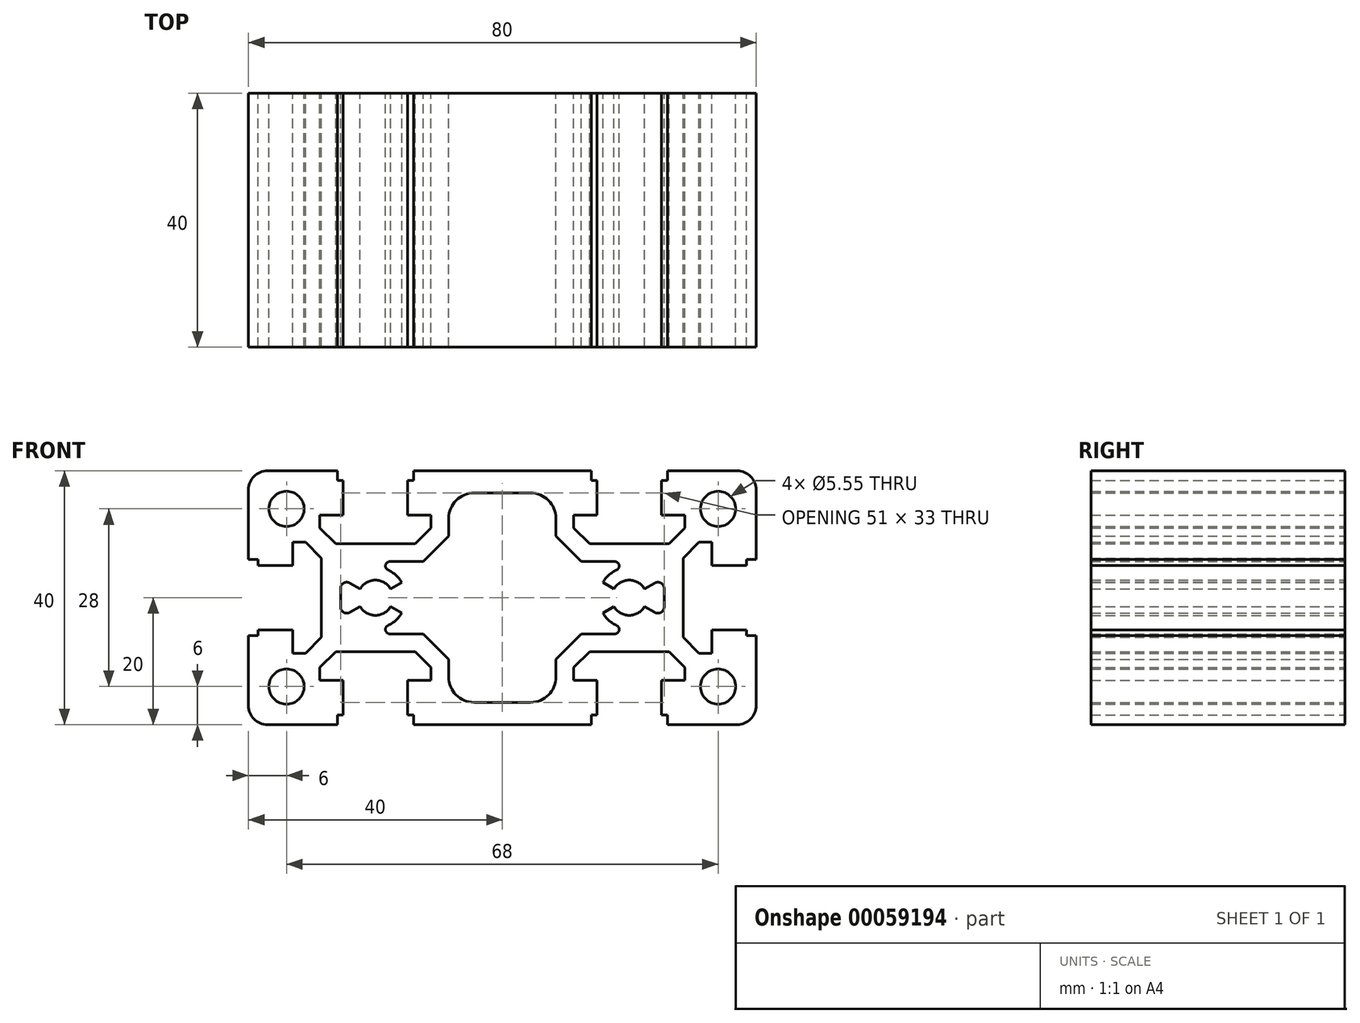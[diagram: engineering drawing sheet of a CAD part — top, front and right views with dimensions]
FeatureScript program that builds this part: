
annotation { "Feature Type Name" : "Feature", "Feature Type Description" : "" }
export const myFeature = defineFeature(function(context is Context, id is Id, definition is map)
    precondition{}
    {
        {
            assignVariable(context, id + "F0", {"name" : "Config", "anyValue" : 0});
        }
        {
            assignVariable(context, id + "F1", {"name" : "Length", "anyValue" : [40, 80, 120, 200, 500][getVariable(context, 'Config')]});
        }
        {
            var Q0;
            Q0=qCreatedBy(makeId("Front.planeOp"),FACE);
            var sketch = newSketch(context, id + "F2", { "sketchPlane" : qUnion([Q0])});
            skLineSegment(sketch, "E0", {"start": v(19.96, 21.75) * mm, "end": v(25.78, 21.75) * mm});
            skLineSegment(sketch, "E1", {"start": v(22.87, 18.84) * mm, "end": v(22.87, 24.66) * mm});
            skLineSegment(sketch, "E2", {"start": v(19.96, 49.75) * mm, "end": v(25.78, 49.75) * mm});
            skLineSegment(sketch, "E3", {"start": v(22.87, 46.84) * mm, "end": v(22.87, 52.66) * mm});
            skLineSegment(sketch, "E4", {"start": v(-48.04, 21.75) * mm, "end": v(-42.22, 21.75) * mm});
            skLineSegment(sketch, "E5", {"start": v(-45.13, 18.84) * mm, "end": v(-45.13, 24.66) * mm});
            skLineSegment(sketch, "E6", {"start": v(-48.04, 49.75) * mm, "end": v(-42.22, 49.75) * mm});
            skLineSegment(sketch, "E7", {"start": v(-45.13, 46.84) * mm, "end": v(-45.13, 52.66) * mm});
            skArc(sketch, "E8", {"start": v(-48.13, 55.75) * mm, "mid": v(-50.25, 54.87) * mm, "end": v(-51.13, 52.75) * mm});
            skLineSegment(sketch, "E9", {"start": v(-51.13, 52.75) * mm, "end": v(-51.13, 41.75) * mm});
            skLineSegment(sketch, "E10", {"start": v(-51.13, 41.75) * mm, "end": v(-49.63, 41.75) * mm});
            skLineSegment(sketch, "E11", {"start": v(-49.63, 41.75) * mm, "end": v(-49.63, 40.85) * mm});
            skLineSegment(sketch, "E12", {"start": v(-49.63, 40.85) * mm, "end": v(-44.13, 40.85) * mm});
            skLineSegment(sketch, "E13", {"start": v(-44.13, 40.85) * mm, "end": v(-44.13, 44.5) * mm});
            skLineSegment(sketch, "E14", {"start": v(-44.13, 44.5) * mm, "end": v(-42.13, 44.5) * mm});
            skLineSegment(sketch, "E15", {"start": v(-42.13, 44.5) * mm, "end": v(-39.63, 42) * mm});
            skLineSegment(sketch, "E16", {"start": v(-39.63, 42) * mm, "end": v(-39.63, 29.5) * mm});
            skLineSegment(sketch, "E17", {"start": v(-39.63, 29.5) * mm, "end": v(-42.13, 27) * mm});
            skLineSegment(sketch, "E18", {"start": v(-42.13, 27) * mm, "end": v(-44.13, 27) * mm});
            skLineSegment(sketch, "E19", {"start": v(-44.13, 27) * mm, "end": v(-44.13, 30.65) * mm});
            skLineSegment(sketch, "E20", {"start": v(-44.13, 30.65) * mm, "end": v(-49.63, 30.65) * mm});
            skLineSegment(sketch, "E21", {"start": v(-49.63, 30.65) * mm, "end": v(-49.63, 29.75) * mm});
            skLineSegment(sketch, "E22", {"start": v(-49.63, 29.75) * mm, "end": v(-51.13, 29.75) * mm});
            skLineSegment(sketch, "E23", {"start": v(-51.13, 29.75) * mm, "end": v(-51.13, 18.75) * mm});
            skArc(sketch, "E24", {"start": v(-51.13, 18.75) * mm, "mid": v(-50.25, 16.63) * mm, "end": v(-48.13, 15.75) * mm});
            skLineSegment(sketch, "E25", {"start": v(-48.13, 15.75) * mm, "end": v(-37.13, 15.75) * mm});
            skLineSegment(sketch, "E26", {"start": v(-37.13, 15.75) * mm, "end": v(-37.13, 17.25) * mm});
            skLineSegment(sketch, "E27", {"start": v(-37.13, 17.25) * mm, "end": v(-36.23, 17.25) * mm});
            skLineSegment(sketch, "E28", {"start": v(-36.23, 17.25) * mm, "end": v(-36.23, 22.75) * mm});
            skLineSegment(sketch, "E29", {"start": v(-36.23, 22.75) * mm, "end": v(-39.88, 22.75) * mm});
            skLineSegment(sketch, "E30", {"start": v(-39.88, 22.75) * mm, "end": v(-39.88, 24.75) * mm});
            skLineSegment(sketch, "E31", {"start": v(-39.88, 24.75) * mm, "end": v(-37.38, 27.25) * mm});
            skLineSegment(sketch, "E32", {"start": v(-37.38, 27.25) * mm, "end": v(-24.88, 27.25) * mm});
            skLineSegment(sketch, "E33", {"start": v(-24.88, 27.25) * mm, "end": v(-22.38, 24.75) * mm});
            skLineSegment(sketch, "E34", {"start": v(-22.38, 24.75) * mm, "end": v(-22.38, 22.75) * mm});
            skLineSegment(sketch, "E35", {"start": v(-22.38, 22.75) * mm, "end": v(-26.03, 22.75) * mm});
            skLineSegment(sketch, "E36", {"start": v(-26.03, 22.75) * mm, "end": v(-26.03, 17.25) * mm});
            skLineSegment(sketch, "E37", {"start": v(-26.03, 17.25) * mm, "end": v(-25.13, 17.25) * mm});
            skLineSegment(sketch, "E38", {"start": v(-25.13, 17.25) * mm, "end": v(-25.13, 15.75) * mm});
            skLineSegment(sketch, "E39", {"start": v(-25.13, 15.75) * mm, "end": v(2.87, 15.75) * mm});
            skLineSegment(sketch, "E40", {"start": v(2.87, 15.75) * mm, "end": v(2.87, 17.25) * mm});
            skLineSegment(sketch, "E41", {"start": v(2.87, 17.25) * mm, "end": v(3.77, 17.25) * mm});
            skLineSegment(sketch, "E42", {"start": v(3.77, 17.25) * mm, "end": v(3.77, 22.75) * mm});
            skLineSegment(sketch, "E43", {"start": v(3.77, 22.75) * mm, "end": v(0.12, 22.75) * mm});
            skLineSegment(sketch, "E44", {"start": v(0.12, 22.75) * mm, "end": v(0.12, 24.75) * mm});
            skLineSegment(sketch, "E45", {"start": v(0.12, 24.75) * mm, "end": v(2.62, 27.25) * mm});
            skLineSegment(sketch, "E46", {"start": v(2.62, 27.25) * mm, "end": v(15.12, 27.25) * mm});
            skLineSegment(sketch, "E47", {"start": v(15.12, 27.25) * mm, "end": v(17.62, 24.75) * mm});
            skLineSegment(sketch, "E48", {"start": v(17.62, 24.75) * mm, "end": v(17.62, 22.75) * mm});
            skLineSegment(sketch, "E49", {"start": v(17.62, 22.75) * mm, "end": v(13.97, 22.75) * mm});
            skLineSegment(sketch, "E50", {"start": v(13.97, 22.75) * mm, "end": v(13.97, 17.25) * mm});
            skLineSegment(sketch, "E51", {"start": v(13.97, 17.25) * mm, "end": v(14.87, 17.25) * mm});
            skLineSegment(sketch, "E52", {"start": v(14.87, 17.25) * mm, "end": v(14.87, 15.75) * mm});
            skLineSegment(sketch, "E53", {"start": v(14.87, 15.75) * mm, "end": v(25.87, 15.75) * mm});
            skArc(sketch, "E54", {"start": v(25.87, 15.75) * mm, "mid": v(28, 16.63) * mm, "end": v(28.87, 18.75) * mm});
            skLineSegment(sketch, "E55", {"start": v(28.87, 18.75) * mm, "end": v(28.87, 29.75) * mm});
            skLineSegment(sketch, "E56", {"start": v(28.87, 29.75) * mm, "end": v(27.37, 29.75) * mm});
            skLineSegment(sketch, "E57", {"start": v(27.37, 29.75) * mm, "end": v(27.37, 30.65) * mm});
            skLineSegment(sketch, "E58", {"start": v(27.37, 30.65) * mm, "end": v(21.87, 30.65) * mm});
            skLineSegment(sketch, "E59", {"start": v(21.87, 30.65) * mm, "end": v(21.87, 27) * mm});
            skLineSegment(sketch, "E60", {"start": v(21.87, 27) * mm, "end": v(19.87, 27) * mm});
            skLineSegment(sketch, "E61", {"start": v(19.87, 27) * mm, "end": v(17.37, 29.5) * mm});
            skLineSegment(sketch, "E62", {"start": v(17.37, 29.5) * mm, "end": v(17.37, 42) * mm});
            skLineSegment(sketch, "E63", {"start": v(17.37, 42) * mm, "end": v(19.87, 44.5) * mm});
            skLineSegment(sketch, "E64", {"start": v(19.87, 44.5) * mm, "end": v(21.87, 44.5) * mm});
            skLineSegment(sketch, "E65", {"start": v(21.87, 44.5) * mm, "end": v(21.87, 40.85) * mm});
            skLineSegment(sketch, "E66", {"start": v(21.87, 40.85) * mm, "end": v(27.37, 40.85) * mm});
            skLineSegment(sketch, "E67", {"start": v(27.37, 40.85) * mm, "end": v(27.37, 41.75) * mm});
            skLineSegment(sketch, "E68", {"start": v(27.37, 41.75) * mm, "end": v(28.87, 41.75) * mm});
            skLineSegment(sketch, "E69", {"start": v(28.87, 41.75) * mm, "end": v(28.87, 52.75) * mm});
            skArc(sketch, "E70", {"start": v(28.87, 52.75) * mm, "mid": v(28, 54.87) * mm, "end": v(25.87, 55.75) * mm});
            skLineSegment(sketch, "E71", {"start": v(25.87, 55.75) * mm, "end": v(14.87, 55.75) * mm});
            skLineSegment(sketch, "E72", {"start": v(14.87, 55.75) * mm, "end": v(14.87, 54.25) * mm});
            skLineSegment(sketch, "E73", {"start": v(14.87, 54.25) * mm, "end": v(13.97, 54.25) * mm});
            skLineSegment(sketch, "E74", {"start": v(13.97, 54.25) * mm, "end": v(13.97, 48.75) * mm});
            skLineSegment(sketch, "E75", {"start": v(13.97, 48.75) * mm, "end": v(17.62, 48.75) * mm});
            skLineSegment(sketch, "E76", {"start": v(17.62, 48.75) * mm, "end": v(17.62, 46.75) * mm});
            skLineSegment(sketch, "E77", {"start": v(17.62, 46.75) * mm, "end": v(15.12, 44.25) * mm});
            skLineSegment(sketch, "E78", {"start": v(15.12, 44.25) * mm, "end": v(2.62, 44.25) * mm});
            skLineSegment(sketch, "E79", {"start": v(2.62, 44.25) * mm, "end": v(0.12, 46.75) * mm});
            skLineSegment(sketch, "E80", {"start": v(0.12, 46.75) * mm, "end": v(0.12, 48.75) * mm});
            skLineSegment(sketch, "E81", {"start": v(0.12, 48.75) * mm, "end": v(3.77, 48.75) * mm});
            skLineSegment(sketch, "E82", {"start": v(3.77, 48.75) * mm, "end": v(3.77, 54.25) * mm});
            skLineSegment(sketch, "E83", {"start": v(3.77, 54.25) * mm, "end": v(2.87, 54.25) * mm});
            skLineSegment(sketch, "E84", {"start": v(2.87, 54.25) * mm, "end": v(2.87, 55.75) * mm});
            skLineSegment(sketch, "E85", {"start": v(2.87, 55.75) * mm, "end": v(-25.13, 55.75) * mm});
            skLineSegment(sketch, "E86", {"start": v(-25.13, 55.75) * mm, "end": v(-25.13, 54.25) * mm});
            skLineSegment(sketch, "E87", {"start": v(-25.13, 54.25) * mm, "end": v(-26.03, 54.25) * mm});
            skLineSegment(sketch, "E88", {"start": v(-26.03, 54.25) * mm, "end": v(-26.03, 48.75) * mm});
            skLineSegment(sketch, "E89", {"start": v(-26.03, 48.75) * mm, "end": v(-22.38, 48.75) * mm});
            skLineSegment(sketch, "E90", {"start": v(-22.38, 48.75) * mm, "end": v(-22.38, 46.75) * mm});
            skLineSegment(sketch, "E91", {"start": v(-22.38, 46.75) * mm, "end": v(-24.88, 44.25) * mm});
            skLineSegment(sketch, "E92", {"start": v(-24.88, 44.25) * mm, "end": v(-37.38, 44.25) * mm});
            skLineSegment(sketch, "E93", {"start": v(-37.38, 44.25) * mm, "end": v(-39.88, 46.75) * mm});
            skLineSegment(sketch, "E94", {"start": v(-39.88, 46.75) * mm, "end": v(-39.88, 48.75) * mm});
            skLineSegment(sketch, "E95", {"start": v(-39.88, 48.75) * mm, "end": v(-36.23, 48.75) * mm});
            skLineSegment(sketch, "E96", {"start": v(-36.23, 48.75) * mm, "end": v(-36.23, 54.25) * mm});
            skLineSegment(sketch, "E97", {"start": v(-36.23, 54.25) * mm, "end": v(-37.13, 54.25) * mm});
            skLineSegment(sketch, "E98", {"start": v(-37.13, 54.25) * mm, "end": v(-37.13, 55.75) * mm});
            skLineSegment(sketch, "E99", {"start": v(-36.63, 37.2) * mm, "end": v(-36.63, 34.3) * mm});
            skArc(sketch, "E100", {"start": v(-35.13, 38.06) * mm, "mid": v(-36.13, 38.06) * mm, "end": v(-36.63, 37.2) * mm});
            skLineSegment(sketch, "E101", {"start": v(-33.53, 37.14) * mm, "end": v(-35.13, 38.06) * mm});
            skArc(sketch, "E102", {"start": v(-28.73, 37.14) * mm, "mid": v(-31.13, 38.53) * mm, "end": v(-33.53, 37.14) * mm});
            skLineSegment(sketch, "E103", {"start": v(-26.97, 38.15) * mm, "end": v(-28.73, 37.14) * mm});
            skArc(sketch, "E104", {"start": v(-26.97, 38.15) * mm, "mid": v(-27.9, 39.3) * mm, "end": v(-29.13, 40.11) * mm});
            skArc(sketch, "E105", {"start": v(-28.84, 41.45) * mm, "mid": v(-29.52, 40.9) * mm, "end": v(-29.13, 40.11) * mm});
            skLineSegment(sketch, "E106", {"start": v(-23.58, 41.45) * mm, "end": v(-28.84, 41.45) * mm});
            skLineSegment(sketch, "E107", {"start": v(-19.58, 45.45) * mm, "end": v(-23.58, 41.45) * mm});
            skLineSegment(sketch, "E108", {"start": v(-19.58, 48.25) * mm, "end": v(-19.58, 45.45) * mm});
            skArc(sketch, "E109", {"start": v(-15.58, 52.25) * mm, "mid": v(-18.4, 51.08) * mm, "end": v(-19.58, 48.25) * mm});
            skLineSegment(sketch, "E110", {"start": v(-6.68, 52.25) * mm, "end": v(-15.58, 52.25) * mm});
            skArc(sketch, "E111", {"start": v(-2.68, 48.25) * mm, "mid": v(-3.85, 51.08) * mm, "end": v(-6.68, 52.25) * mm});
            skLineSegment(sketch, "E112", {"start": v(-2.68, 45.45) * mm, "end": v(-2.68, 48.25) * mm});
            skLineSegment(sketch, "E113", {"start": v(1.32, 41.45) * mm, "end": v(-2.68, 45.45) * mm});
            skLineSegment(sketch, "E114", {"start": v(6.58, 41.45) * mm, "end": v(1.32, 41.45) * mm});
            skArc(sketch, "E115", {"start": v(6.87, 40.11) * mm, "mid": v(7.26, 40.9) * mm, "end": v(6.58, 41.45) * mm});
            skArc(sketch, "E116", {"start": v(6.87, 40.11) * mm, "mid": v(5.64, 39.3) * mm, "end": v(4.71, 38.15) * mm});
            skLineSegment(sketch, "E117", {"start": v(6.47, 37.14) * mm, "end": v(4.71, 38.15) * mm});
            skArc(sketch, "E118", {"start": v(11.27, 37.14) * mm, "mid": v(8.87, 38.53) * mm, "end": v(6.47, 37.14) * mm});
            skLineSegment(sketch, "E119", {"start": v(12.87, 38.06) * mm, "end": v(11.27, 37.14) * mm});
            skArc(sketch, "E120", {"start": v(14.37, 37.2) * mm, "mid": v(13.87, 38.06) * mm, "end": v(12.87, 38.06) * mm});
            skLineSegment(sketch, "E121", {"start": v(14.37, 34.3) * mm, "end": v(14.37, 37.2) * mm});
            skArc(sketch, "E122", {"start": v(12.87, 33.44) * mm, "mid": v(13.87, 33.44) * mm, "end": v(14.37, 34.3) * mm});
            skLineSegment(sketch, "E123", {"start": v(11.27, 34.36) * mm, "end": v(12.87, 33.44) * mm});
            skArc(sketch, "E124", {"start": v(6.47, 34.36) * mm, "mid": v(8.87, 32.98) * mm, "end": v(11.27, 34.36) * mm});
            skLineSegment(sketch, "E125", {"start": v(4.71, 33.35) * mm, "end": v(6.47, 34.36) * mm});
            skArc(sketch, "E126", {"start": v(4.71, 33.35) * mm, "mid": v(5.64, 32.2) * mm, "end": v(6.87, 31.39) * mm});
            skArc(sketch, "E127", {"start": v(6.58, 30.05) * mm, "mid": v(7.26, 30.6) * mm, "end": v(6.87, 31.39) * mm});
            skLineSegment(sketch, "E128", {"start": v(1.32, 30.05) * mm, "end": v(6.58, 30.05) * mm});
            skLineSegment(sketch, "E129", {"start": v(-2.68, 26.05) * mm, "end": v(1.32, 30.05) * mm});
            skLineSegment(sketch, "E130", {"start": v(-2.68, 23.25) * mm, "end": v(-2.68, 26.05) * mm});
            skArc(sketch, "E131", {"start": v(-6.68, 19.25) * mm, "mid": v(-3.85, 20.42) * mm, "end": v(-2.68, 23.25) * mm});
            skLineSegment(sketch, "E132", {"start": v(-15.58, 19.25) * mm, "end": v(-6.68, 19.25) * mm});
            skArc(sketch, "E133", {"start": v(-19.58, 23.25) * mm, "mid": v(-18.4, 20.42) * mm, "end": v(-15.58, 19.25) * mm});
            skLineSegment(sketch, "E134", {"start": v(-19.58, 26.05) * mm, "end": v(-19.58, 23.25) * mm});
            skLineSegment(sketch, "E135", {"start": v(-23.58, 30.05) * mm, "end": v(-19.58, 26.05) * mm});
            skLineSegment(sketch, "E136", {"start": v(-28.84, 30.05) * mm, "end": v(-23.58, 30.05) * mm});
            skArc(sketch, "E137", {"start": v(-29.13, 31.39) * mm, "mid": v(-29.52, 30.6) * mm, "end": v(-28.84, 30.05) * mm});
            skArc(sketch, "E138", {"start": v(-29.13, 31.39) * mm, "mid": v(-27.9, 32.2) * mm, "end": v(-26.97, 33.35) * mm});
            skLineSegment(sketch, "E139", {"start": v(-28.73, 34.36) * mm, "end": v(-26.97, 33.35) * mm});
            skArc(sketch, "E140", {"start": v(-33.53, 34.36) * mm, "mid": v(-31.13, 32.98) * mm, "end": v(-28.73, 34.36) * mm});
            skLineSegment(sketch, "E141", {"start": v(-35.13, 33.44) * mm, "end": v(-33.53, 34.36) * mm});
            skCircle(sketch, "E142", {"center": v(22.87, 21.75) * mm, "radius": 2.77 * mm});
            skCircle(sketch, "E143", {"center": v(22.87, 49.75) * mm, "radius": 2.77 * mm});
            skArc(sketch, "E144", {"start": v(-36.63, 34.3) * mm, "mid": v(-36.13, 33.44) * mm, "end": v(-35.13, 33.44) * mm});
            skCircle(sketch, "E145", {"center": v(-45.13, 21.75) * mm, "radius": 2.77 * mm});
            skCircle(sketch, "E146", {"center": v(-45.13, 49.75) * mm, "radius": 2.77 * mm});
            skLineSegment(sketch, "E147", {"start": v(-37.13, 55.75) * mm, "end": v(-48.13, 55.75) * mm});
            skLineSegment(sketch, "E148", {"start": v(-11.13, 15.75) * mm, "end": v(-11.13, 55.75) * mm, "construction": true});
            skPoint(sketch, "E149", {"position": v(-11.13, 35.75) * mm});
            skSolve(sketch);
        }
        {
            var Q0;
            Q0=makeQuery(id+"F2.imprint","IMPRINT",FACE,{"disambiguationData":[TD([[makeQuery(id+"F2.imprint","IMPRINT",EDGE,{"derivedFrom":sQuery(id+"F2.wireOp",EDGE,"E8")}),1.0]])]});
            extrude(context, id + "F3", {"entities" : qUnion([Q0]), "depth" : (getVariable(context, 'Length')) * mm});
        }
        {
            var Q0;
            Q0=makeQuery(id+"F3.opExtrude","SWEPT_BODY",BODY,{"disambiguationData":[OSD([sQuery(id+"F2.wireOp",EDGE,"E8"),sQuery(id+"F2.wireOp",EDGE,"E9"),sQuery(id+"F2.wireOp",EDGE,"E10"),sQuery(id+"F2.wireOp",EDGE,"E11"),sQuery(id+"F2.wireOp",EDGE,"E12"),sQuery(id+"F2.wireOp",EDGE,"E13"),sQuery(id+"F2.wireOp",EDGE,"E14"),sQuery(id+"F2.wireOp",EDGE,"E15"),sQuery(id+"F2.wireOp",EDGE,"E16"),sQuery(id+"F2.wireOp",EDGE,"E17"),sQuery(id+"F2.wireOp",EDGE,"E18"),sQuery(id+"F2.wireOp",EDGE,"E19"),sQuery(id+"F2.wireOp",EDGE,"E20"),sQuery(id+"F2.wireOp",EDGE,"E21"),sQuery(id+"F2.wireOp",EDGE,"E22"),sQuery(id+"F2.wireOp",EDGE,"E23"),sQuery(id+"F2.wireOp",EDGE,"E24"),sQuery(id+"F2.wireOp",EDGE,"E25"),sQuery(id+"F2.wireOp",EDGE,"E26"),sQuery(id+"F2.wireOp",EDGE,"E27"),sQuery(id+"F2.wireOp",EDGE,"E28"),sQuery(id+"F2.wireOp",EDGE,"E29"),sQuery(id+"F2.wireOp",EDGE,"E30"),sQuery(id+"F2.wireOp",EDGE,"E31"),sQuery(id+"F2.wireOp",EDGE,"E32"),sQuery(id+"F2.wireOp",EDGE,"E33"),sQuery(id+"F2.wireOp",EDGE,"E34"),sQuery(id+"F2.wireOp",EDGE,"E35"),sQuery(id+"F2.wireOp",EDGE,"E36"),sQuery(id+"F2.wireOp",EDGE,"E37"),sQuery(id+"F2.wireOp",EDGE,"E38"),sQuery(id+"F2.wireOp",EDGE,"E39"),sQuery(id+"F2.wireOp",EDGE,"E40"),sQuery(id+"F2.wireOp",EDGE,"E41"),sQuery(id+"F2.wireOp",EDGE,"E42"),sQuery(id+"F2.wireOp",EDGE,"E43"),sQuery(id+"F2.wireOp",EDGE,"E44"),sQuery(id+"F2.wireOp",EDGE,"E45"),sQuery(id+"F2.wireOp",EDGE,"E46"),sQuery(id+"F2.wireOp",EDGE,"E47"),sQuery(id+"F2.wireOp",EDGE,"E48"),sQuery(id+"F2.wireOp",EDGE,"E49"),sQuery(id+"F2.wireOp",EDGE,"E50"),sQuery(id+"F2.wireOp",EDGE,"E51"),sQuery(id+"F2.wireOp",EDGE,"E52"),sQuery(id+"F2.wireOp",EDGE,"E53"),sQuery(id+"F2.wireOp",EDGE,"E54"),sQuery(id+"F2.wireOp",EDGE,"E55"),sQuery(id+"F2.wireOp",EDGE,"E56"),sQuery(id+"F2.wireOp",EDGE,"E57"),sQuery(id+"F2.wireOp",EDGE,"E58"),sQuery(id+"F2.wireOp",EDGE,"E59"),sQuery(id+"F2.wireOp",EDGE,"E60"),sQuery(id+"F2.wireOp",EDGE,"E61"),sQuery(id+"F2.wireOp",EDGE,"E62"),sQuery(id+"F2.wireOp",EDGE,"E63"),sQuery(id+"F2.wireOp",EDGE,"E64"),sQuery(id+"F2.wireOp",EDGE,"E65"),sQuery(id+"F2.wireOp",EDGE,"E66"),sQuery(id+"F2.wireOp",EDGE,"E67"),sQuery(id+"F2.wireOp",EDGE,"E68"),sQuery(id+"F2.wireOp",EDGE,"E69"),sQuery(id+"F2.wireOp",EDGE,"E70"),sQuery(id+"F2.wireOp",EDGE,"E71"),sQuery(id+"F2.wireOp",EDGE,"E72"),sQuery(id+"F2.wireOp",EDGE,"E73"),sQuery(id+"F2.wireOp",EDGE,"E74"),sQuery(id+"F2.wireOp",EDGE,"E75"),sQuery(id+"F2.wireOp",EDGE,"E76"),sQuery(id+"F2.wireOp",EDGE,"E77"),sQuery(id+"F2.wireOp",EDGE,"E78"),sQuery(id+"F2.wireOp",EDGE,"E79"),sQuery(id+"F2.wireOp",EDGE,"E80"),sQuery(id+"F2.wireOp",EDGE,"E81"),sQuery(id+"F2.wireOp",EDGE,"E82"),sQuery(id+"F2.wireOp",EDGE,"E83"),sQuery(id+"F2.wireOp",EDGE,"E84"),sQuery(id+"F2.wireOp",EDGE,"E85"),sQuery(id+"F2.wireOp",EDGE,"E86"),sQuery(id+"F2.wireOp",EDGE,"E87"),sQuery(id+"F2.wireOp",EDGE,"E88"),sQuery(id+"F2.wireOp",EDGE,"E89"),sQuery(id+"F2.wireOp",EDGE,"E90"),sQuery(id+"F2.wireOp",EDGE,"E91"),sQuery(id+"F2.wireOp",EDGE,"E92"),sQuery(id+"F2.wireOp",EDGE,"E93"),sQuery(id+"F2.wireOp",EDGE,"E94"),sQuery(id+"F2.wireOp",EDGE,"E95"),sQuery(id+"F2.wireOp",EDGE,"E96"),sQuery(id+"F2.wireOp",EDGE,"E97"),sQuery(id+"F2.wireOp",EDGE,"E98"),sQuery(id+"F2.wireOp",EDGE,"E99"),sQuery(id+"F2.wireOp",EDGE,"E100"),sQuery(id+"F2.wireOp",EDGE,"E101"),sQuery(id+"F2.wireOp",EDGE,"E102"),sQuery(id+"F2.wireOp",EDGE,"E103"),sQuery(id+"F2.wireOp",EDGE,"E104"),sQuery(id+"F2.wireOp",EDGE,"E105"),sQuery(id+"F2.wireOp",EDGE,"E106"),sQuery(id+"F2.wireOp",EDGE,"E107"),sQuery(id+"F2.wireOp",EDGE,"E108"),sQuery(id+"F2.wireOp",EDGE,"E109"),sQuery(id+"F2.wireOp",EDGE,"E110"),sQuery(id+"F2.wireOp",EDGE,"E111"),sQuery(id+"F2.wireOp",EDGE,"E112"),sQuery(id+"F2.wireOp",EDGE,"E113"),sQuery(id+"F2.wireOp",EDGE,"E114"),sQuery(id+"F2.wireOp",EDGE,"E115"),sQuery(id+"F2.wireOp",EDGE,"E116"),sQuery(id+"F2.wireOp",EDGE,"E117"),sQuery(id+"F2.wireOp",EDGE,"E118"),sQuery(id+"F2.wireOp",EDGE,"E119"),sQuery(id+"F2.wireOp",EDGE,"E120"),sQuery(id+"F2.wireOp",EDGE,"E121"),sQuery(id+"F2.wireOp",EDGE,"E122"),sQuery(id+"F2.wireOp",EDGE,"E123"),sQuery(id+"F2.wireOp",EDGE,"E124"),sQuery(id+"F2.wireOp",EDGE,"E125"),sQuery(id+"F2.wireOp",EDGE,"E126"),sQuery(id+"F2.wireOp",EDGE,"E127"),sQuery(id+"F2.wireOp",EDGE,"E128"),sQuery(id+"F2.wireOp",EDGE,"E129"),sQuery(id+"F2.wireOp",EDGE,"E130"),sQuery(id+"F2.wireOp",EDGE,"E131"),sQuery(id+"F2.wireOp",EDGE,"E132"),sQuery(id+"F2.wireOp",EDGE,"E133"),sQuery(id+"F2.wireOp",EDGE,"E134"),sQuery(id+"F2.wireOp",EDGE,"E135"),sQuery(id+"F2.wireOp",EDGE,"E136"),sQuery(id+"F2.wireOp",EDGE,"E137"),sQuery(id+"F2.wireOp",EDGE,"E138"),sQuery(id+"F2.wireOp",EDGE,"E139"),sQuery(id+"F2.wireOp",EDGE,"E140"),sQuery(id+"F2.wireOp",EDGE,"E141"),sQuery(id+"F2.wireOp",EDGE,"E142"),sQuery(id+"F2.wireOp",EDGE,"E143"),sQuery(id+"F2.wireOp",EDGE,"E144"),sQuery(id+"F2.wireOp",EDGE,"E145"),sQuery(id+"F2.wireOp",EDGE,"E146"),sQuery(id+"F2.wireOp",EDGE,"E147")])]});
            var Q1;
            Q1=sQuery(id+"F2.wireOp",VERTEX,"E149");
            var Q2;
            Q2=qCreatedBy(makeId("Origin.pointOp"),VERTEX);
            transform(context, id + "F4", {"entities" : qUnion([Q0]), "transformType" : TransformType.TRANSLATION_ENTITY, "oppositeDirectionEntity" : false, "transformLine" : qUnion([Q1, Q2]), "makeCopy" : false});
        }
    });
